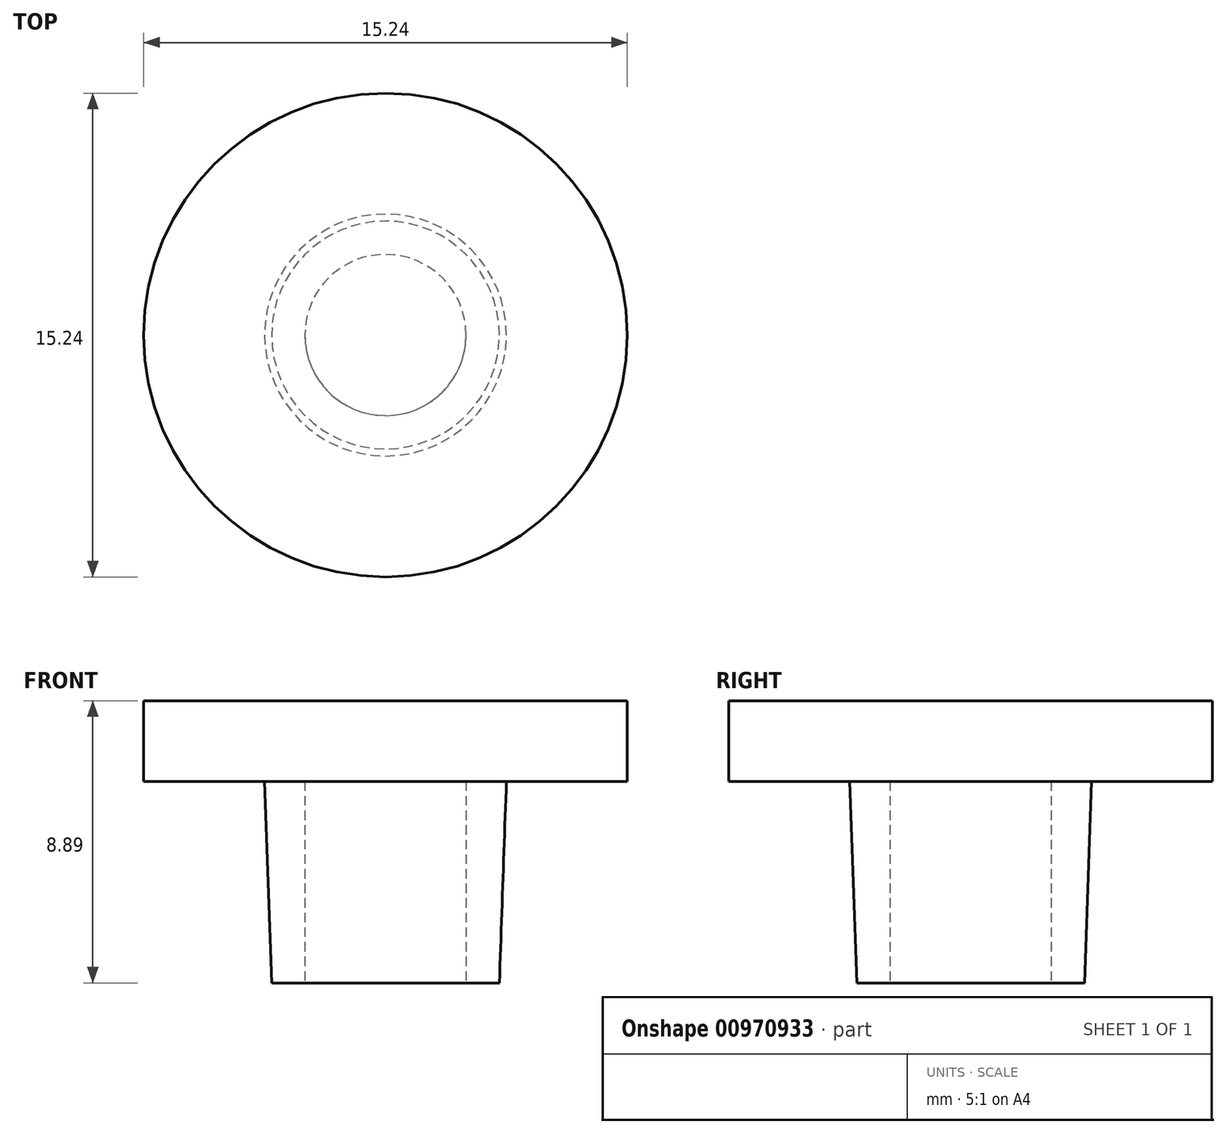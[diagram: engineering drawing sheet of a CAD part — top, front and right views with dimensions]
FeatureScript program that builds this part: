
annotation { "Feature Type Name" : "Feature", "Feature Type Description" : "" }
export const myFeature = defineFeature(function(context is Context, id is Id, definition is map)
    precondition{}
    {
        {
            var Q0;
            Q0=qCreatedBy(makeId("Top.planeOp"),FACE);
            var sketch = newSketch(context, id + "F0", { "sketchPlane" : qUnion([Q0])});
            skCircle(sketch, "E0", {"center": v(0, 0) * mm, "radius": 7.62 * mm});
            skSolve(sketch);
        }
        {
            var Q0;
            Q0=makeQuery(id+"F0.imprint","IMPRINT",FACE,{"disambiguationData":[TD([[makeQuery(id+"F0.imprint","IMPRINT",EDGE,{"derivedFrom":sQuery(id+"F0.wireOp",EDGE,"E0")}),1.0]])]});
            extrude(context, id + "F1", {"entities" : qUnion([Q0]), "depth" : 2.54 * mm, "offsetDistance" : 25.4 * mm});
        }
        {
            var Q0;
            Q0=qCreatedBy(makeId("Top.planeOp"),FACE);
            var sketch = newSketch(context, id + "F2", { "sketchPlane" : qUnion([Q0])});
            skCircle(sketch, "E1", {"center": v(0, 0) * mm, "radius": 3.81 * mm});
            skSolve(sketch);
        }
        {
            var Q0;
            Q0=qSketchRegion(id+"F2",true);
            var Q1;
            Q1=sQuery(id+"F2.wireOp",EDGE,"E1");
            extrude(context, id + "F3", {"entities" : qUnion([Q0]), "operationType" : NewBodyOperationType.ADD, "surfaceEntities" : qUnion([Q1]), "oppositeDirection" : true, "depth" : 6.35 * mm, "offsetDistance" : 25.4 * mm, "hasDraft" : true, "draftAngle" : 2 * degree, "draftPullDirection" : true});
        }
        {
            var Q0;
            Q0=makeQuery(id+"F3.opExtrude","CAP_FACE",FACE,{"disambiguationData":[OSD([sQuery(id+"F2.wireOp",EDGE,"E1")])],"isStart":false});
            var sketch = newSketch(context, id + "F4", { "sketchPlane" : qUnion([Q0])});
            skCircle(sketch, "E2", {"center": v(0, 0) * mm, "radius": 2.54 * mm});
            skSolve(sketch);
        }
        {
            var Q0;
            Q0=qSketchRegion(id+"F4",true);
            var Q1;
            Q1=makeQuery(id+"F1.opExtrude","CAP_FACE",FACE,{"disambiguationData":[OSD([sQuery(id+"F0.wireOp",EDGE,"E0")])],"isStart":true});
            extrude(context, id + "F5", {"entities" : qUnion([Q0]), "operationType" : NewBodyOperationType.REMOVE, "endBound" : BoundingType.UP_TO_SURFACE, "oppositeDirection" : true, "depth" : 25.4 * mm, "endBoundEntityFace" : qUnion([Q1]), "offsetDistance" : 25.4 * mm});
        }
    });
